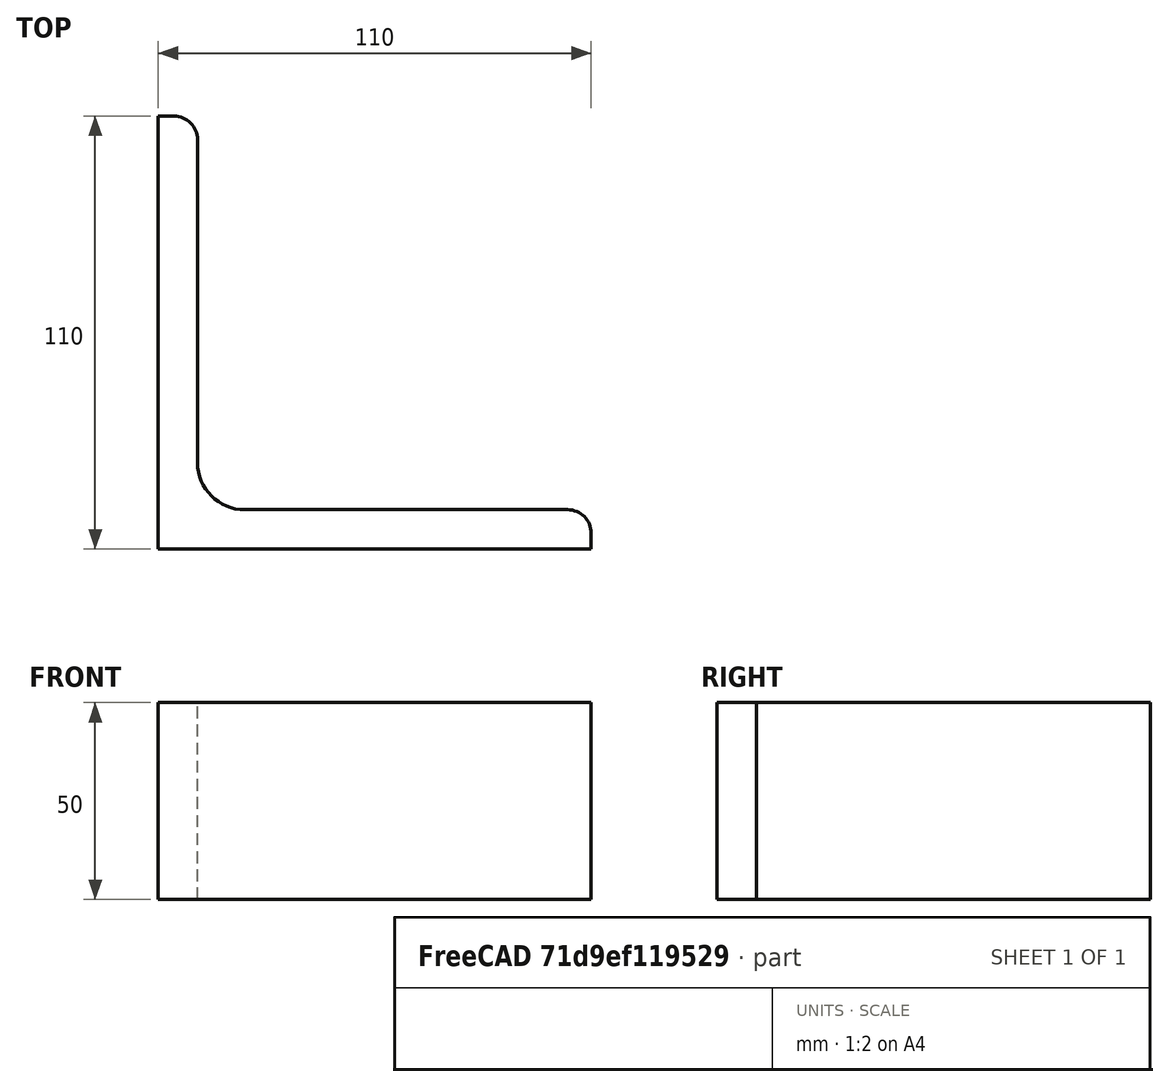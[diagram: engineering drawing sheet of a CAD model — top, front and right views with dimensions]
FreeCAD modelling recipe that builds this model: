
FCSTD DOCUMENT  (FreeCAD 0.15R4671 (Git))
Label: Angle Bar L110x110x10 EN10056 S235JR
License: All rights reserved
LicenseURL: http://en.wikipedia.org/wiki/All_rights_reserved
objects: Sketcher::SketchObject×1, Part::Extrusion×1
note: 2 computed .brp shape members not serialized (recipe doc carries the construction recipe); baked Part::Feature solids carry a one-line shape summary decoded from their .brp

FEATURE [Sketcher::SketchObject] Sketch
  sketch-geometry (9):
    g0: LineSegment StartX=0 StartY=0 StartZ=0 EndX=110 EndY=0 EndZ=0
    g1: LineSegment StartX=110 StartY=0 StartZ=0 EndX=110 EndY=4 EndZ=0
    g2: LineSegment StartX=104 StartY=10 StartZ=0 EndX=22 EndY=10 EndZ=0
    g3: LineSegment StartX=0 StartY=0 StartZ=0 EndX=0 EndY=110 EndZ=0
    g4: LineSegment StartX=0 StartY=110 StartZ=0 EndX=4 EndY=110 EndZ=0
    g5: LineSegment StartX=10 StartY=104 StartZ=0 EndX=10 EndY=22 EndZ=0
    g6: ArcOfCircle CenterX=22 CenterY=22 CenterZ=0 NormalX=0 NormalY=0 NormalZ=1 Radius=12 StartAngle=3.14159 EndAngle=4.71239
    g7: ArcOfCircle CenterX=4 CenterY=104 CenterZ=0 NormalX=0 NormalY=0 NormalZ=1 Radius=6 StartAngle=0 EndAngle=1.5708
    g8: ArcOfCircle CenterX=104 CenterY=4 CenterZ=0 NormalX=0 NormalY=0 NormalZ=1 Radius=6 StartAngle=0 EndAngle=1.5708
  constraints (23):
    c: Coincident(g0,g-1)
    c: Horizontal(g0)
    c: Coincident(g1,g0)
    c: Vertical(g1)
    c: Horizontal(g2)
    c: Coincident(g3,g-1)
    c: Vertical(g3)
    c: Coincident(g4,g3)
    c: Horizontal(g4)
    c: Vertical(g5)
    c: Tangent(g5,g6) = -1.5708
    c: Tangent(g2,g6) = 1.5708
    c: Tangent(g4,g7) = 1.5708
    c: Tangent(g5,g7) = 1.5708
    c: Tangent(g2,g8) = -1.5708
    c: Tangent(g1,g8) = -1.5708
    c: DistanceX(g0) = 110
    c: DistanceY(g3) = 110
    c: DistanceY(g0,g2) = 10
    c: DistanceX(g3,g5) = 10
    c: Radius(g6) = 12
    c: Radius(g8) = 6
    c: Radius(g7) = 6
FEATURE [Part::Extrusion] Extrude  label="Angle Bar L110x110x10 EN10056 S235JR"
  Base = -> Sketch
  Dir = (0,0,50)
  Solid = true
